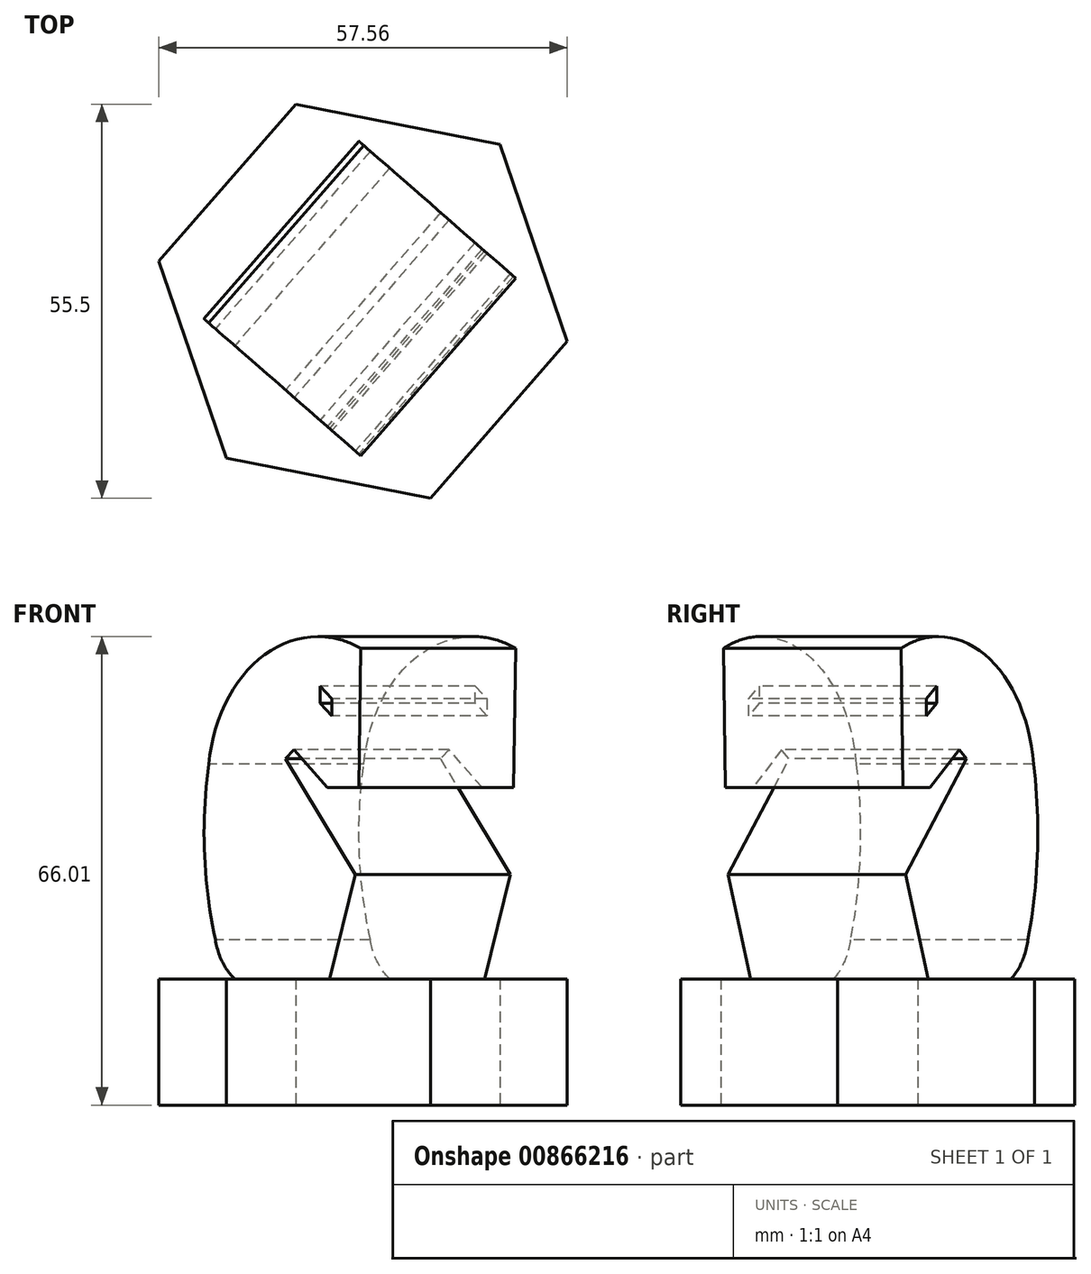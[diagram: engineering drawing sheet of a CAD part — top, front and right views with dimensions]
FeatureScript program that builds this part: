
annotation { "Feature Type Name" : "Feature", "Feature Type Description" : "" }
export const myFeature = defineFeature(function(context is Context, id is Id, definition is map)
    precondition{}
    {
        {
            var Q0;
            Q0=qCreatedBy(makeId("Top.planeOp"),FACE);
            var sketch = newSketch(context, id + "F0", { "sketchPlane" : qUnion([Q0])});
            skCircle(sketch, "E0.cCircle", {"center": v(0, 0) * mm, "radius": 25.4 * mm, "construction": true});
            skLineSegment(sketch, "E0.0", {"start": v(-28.78, 5.65) * mm, "end": v(-9.5, 27.75) * mm});
            skLineSegment(sketch, "E0.1", {"start": v(-9.5, 27.75) * mm, "end": v(19.29, 22.1) * mm});
            skLineSegment(sketch, "E0.2", {"start": v(19.29, 22.1) * mm, "end": v(28.78, -5.65) * mm});
            skLineSegment(sketch, "E0.3", {"start": v(28.78, -5.65) * mm, "end": v(9.5, -27.75) * mm});
            skLineSegment(sketch, "E0.4", {"start": v(9.5, -27.75) * mm, "end": v(-19.29, -22.1) * mm});
            skLineSegment(sketch, "E0.5", {"start": v(-19.29, -22.1) * mm, "end": v(-28.78, 5.65) * mm});
            skPoint(sketch, "E0.0.midPoint", {"position": v(-19.14, 16.7) * mm});
            skSolve(sketch);
        }
        {
            var Q0;
            Q0 = qSketchRegion(id + "F0", true);
            extrude(context, id + "F1", {"entities" : qUnion([Q0]), "depth" : 17.78 * mm, "offsetDistance" : 25.4 * mm});
        }
        {
            var Q0;
            Q0=makeQuery(id+"F1.opExtrude","CAP_FACE",FACE,{"disambiguationData":[OSD([sQuery(id+"F0.wireOp",EDGE,"E0.0"),sQuery(id+"F0.wireOp",EDGE,"E0.1"),sQuery(id+"F0.wireOp",EDGE,"E0.2"),sQuery(id+"F0.wireOp",EDGE,"E0.3"),sQuery(id+"F0.wireOp",EDGE,"E0.4"),sQuery(id+"F0.wireOp",EDGE,"E0.5")])],"isStart":false});
            var sketch = newSketch(context, id + "F2", { "sketchPlane" : qUnion([Q0])});
            skCircle(sketch, "E1.cCircle", {"center": v(0, 0) * mm, "radius": 16.6 * mm, "construction": true});
            skLineSegment(sketch, "E1.0", {"start": v(-23.43, -1.6) * mm, "end": v(-1.6, 23.43) * mm});
            skLineSegment(sketch, "E1.1", {"start": v(-1.6, 23.43) * mm, "end": v(23.43, 1.6) * mm});
            skLineSegment(sketch, "E1.2", {"start": v(23.43, 1.6) * mm, "end": v(1.6, -23.43) * mm});
            skLineSegment(sketch, "E1.3", {"start": v(1.6, -23.43) * mm, "end": v(-23.43, -1.6) * mm});
            skPoint(sketch, "E1.0.midPoint", {"position": v(-12.5, 10.92) * mm});
            skSolve(sketch);
        }
        {
            var Q0;
            Q0 = qSketchRegion(id + "F2", true);
            extrude(context, id + "F3", {"entities" : qUnion([Q0]), "operationType" : NewBodyOperationType.ADD, "depth" : 50.8 * mm, "offsetDistance" : 25.4 * mm});
        }
        {
            var Q0;
            Q0=makeQuery(id+"F3.opExtrude","SWEPT_FACE",FACE,{"disambiguationData":[OSD([sQuery(id+"F2.wireOp",EDGE,"E1.3")])]});
            var sketch = newSketch(context, id + "F4", { "sketchPlane" : qUnion([Q0])});
            skLineSegment(sketch, "E2", {"start": v(13.07, 32.48) * mm, "end": v(0, 48.78) * mm});
            skLineSegment(sketch, "E3", {"start": v(0, 48.78) * mm, "end": v(1.6, 50.07) * mm});
            skLineSegment(sketch, "E4", {"start": v(1.6, 50.07) * mm, "end": v(7.81, 44.72) * mm});
            skLineSegment(sketch, "E5", {"start": v(7.81, 44.72) * mm, "end": v(13.68, 44.72) * mm});
            skLineSegment(sketch, "E6", {"start": v(13.68, 44.72) * mm, "end": v(14.07, 64.37) * mm});
            skLineSegment(sketch, "E7", {"start": v(13.07, 32.48) * mm, "end": v(8.22, 17.78) * mm});
            skArc(sketch, "E8", {"start": v(14.07, 64.37) * mm, "mid": v(-4.2, 63.3) * mm, "end": v(-14.36, 48.06) * mm});
            skArc(sketch, "E9", {"start": v(-14.36, 48.06) * mm, "mid": v(-15.17, 35.6) * mm, "end": v(-13.11, 23.3) * mm});
            skLineSegment(sketch, "E10", {"start": v(-9.5, 17.78) * mm, "end": v(8.22, 17.78) * mm});
            skArc(sketch, "E11", {"start": v(-13.11, 23.3) * mm, "mid": v(-11.84, 20.2) * mm, "end": v(-9.5, 17.78) * mm});
            skSolve(sketch);
        }
        {
            var Q0;
            {var subQ4=sQuery(id+"F4.wireOp",EDGE,"uQNwh9YD-Gbbu-foxB-lbe9-PbJ4YUwcdE2G");Q0=makeQuery(id+"F4.imprint","IMPRINT",FACE,{"disambiguationData":[TD([[makeQuery(id+"F4.imprint","IMPRINT",EDGE,{"derivedFrom":subQ4}),-1.0]])]});}
            var Q1;
            Q1=makeQuery(id+"F4.imprint","IMPRINT",FACE,{"disambiguationData":[TD([[makeQuery(id+"F4.imprint","IMPRINT",EDGE,{"derivedFrom":sQuery(id+"F4.wireOp",EDGE,"E2")}),-1.0]])]});
            extrude(context, id + "F5", {"entities" : qUnion([Q0, Q1]), "operationType" : NewBodyOperationType.REMOVE, "oppositeDirection" : true, "depth" : 76.2 * mm, "offsetDistance" : 25.4 * mm});
        }
        {
            var Q0;
            Q0=makeQuery(id+"F3.opExtrude","SWEPT_FACE",FACE,{"disambiguationData":[OSD([sQuery(id+"F2.wireOp",EDGE,"E1.3")])]});
            var sketch = newSketch(context, id + "F6", { "sketchPlane" : qUnion([Q0])});
            skLineSegment(sketch, "E12", {"start": v(6.46, 59.04) * mm, "end": v(6.46, 56.65) * mm});
            skLineSegment(sketch, "E13", {"start": v(6.46, 56.65) * mm, "end": v(8.67, 54.86) * mm});
            skLineSegment(sketch, "E14", {"start": v(8.67, 54.86) * mm, "end": v(8.67, 57.25) * mm});
            skLineSegment(sketch, "E15", {"start": v(8.67, 57.25) * mm, "end": v(6.46, 59.04) * mm});
            skSolve(sketch);
        }
        {
            var Q0;
            Q0 = qSketchRegion(id + "F6", true);
            extrude(context, id + "F7", {"entities" : qUnion([Q0]), "operationType" : NewBodyOperationType.REMOVE, "oppositeDirection" : true, "depth" : 177.8 * mm, "offsetDistance" : 25.4 * mm});
        }
        {
            var Q0;
            Q0 = qSketchRegion(id + "F6", true);
            extrude(context, id + "F8", {"entities" : qUnion([Q0]), "operationType" : NewBodyOperationType.REMOVE, "oppositeDirection" : true, "depth" : 177.8 * mm, "offsetDistance" : 25.4 * mm});
        }
    });
